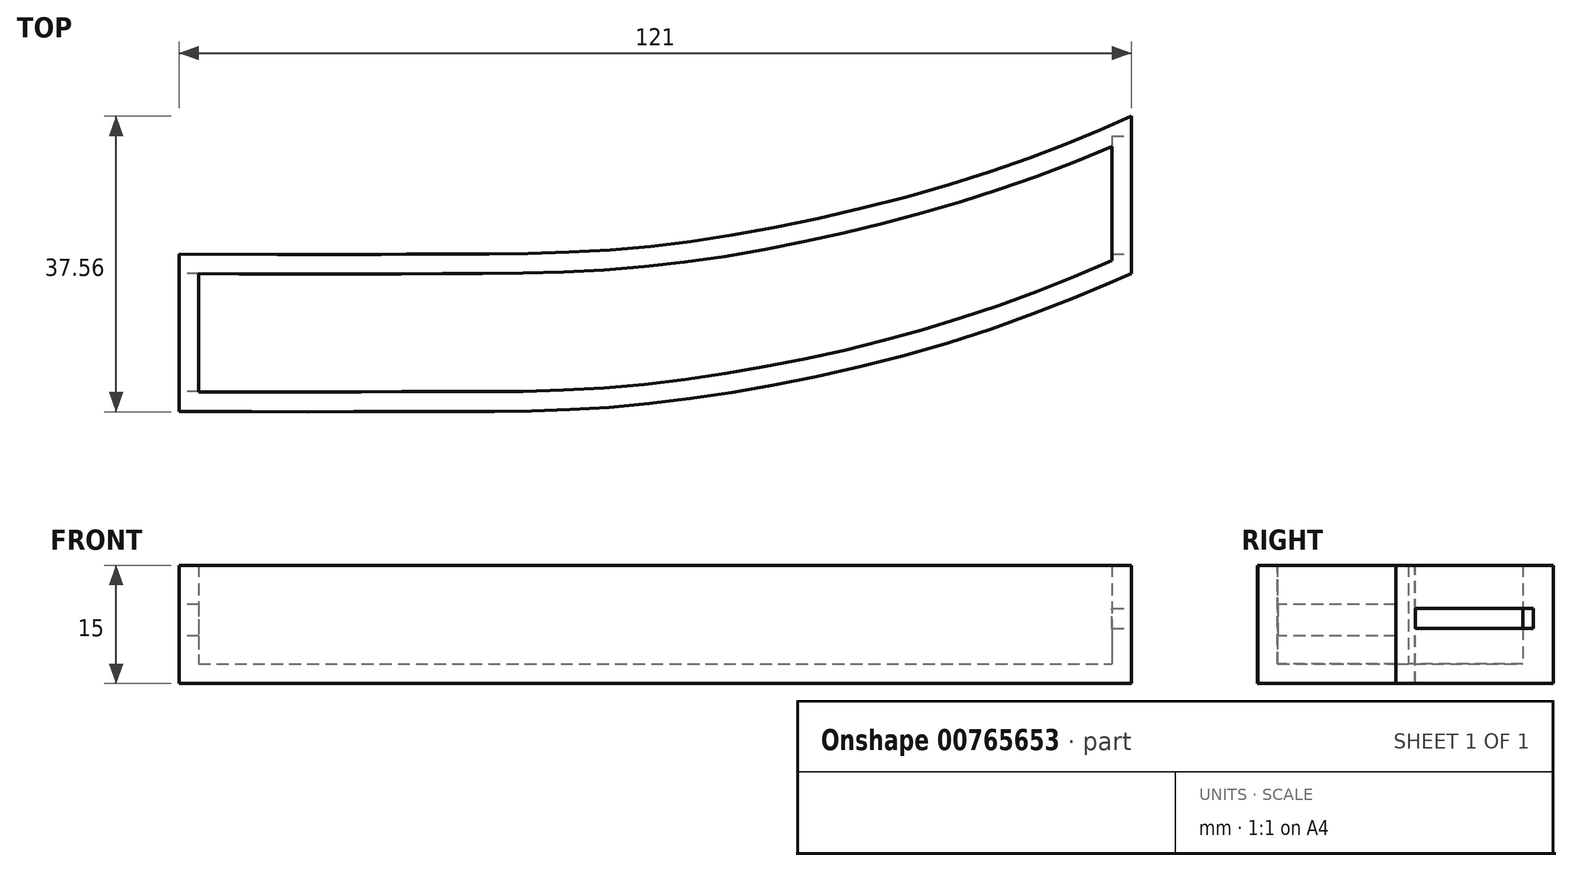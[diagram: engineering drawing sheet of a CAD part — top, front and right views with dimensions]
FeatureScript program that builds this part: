
annotation { "Feature Type Name" : "Feature", "Feature Type Description" : "" }
export const myFeature = defineFeature(function(context is Context, id is Id, definition is map)
    precondition{}
    {
        {
            var Q0;
            Q0=qCreatedBy(makeId("Top.planeOp"),FACE);
            var sketch = newSketch(context, id + "F0", { "sketchPlane" : qUnion([Q0])});
            skPoint(sketch, "E0.1.internal.orphan", {"position": v(32.6, 20) * mm});
            skPoint(sketch, "E0.2.internal.orphan", {"position": v(51.37, 20.3) * mm});
            skPoint(sketch, "E0.3.internal.orphan", {"position": v(102.14, 30.14) * mm});
            skPoint(sketch, "E0.5.internal.orphan", {"position": v(121, 37.5) * mm});
            skPoint(sketch, "E0.start.orphan", {"position": v(0, 20) * mm});
            skFitSpline(sketch, "E1", {"points": [v(0, 20) * mm, v(32.6, 20) * mm, v(51.37, 20.3) * mm, v(75, 23.23) * mm, v(102.14, 30.14) * mm, v(121, 37.5) * mm], "startDerivative": vector(347.02, -2.36) * mm, "endDerivative": vector(89.93, 40.6) * mm});
            skPoint(sketch, "E2.1.internal.orphan", {"position": v(32.6, 0) * mm});
            skPoint(sketch, "E2.2.internal.orphan", {"position": v(51.37, 0.3) * mm});
            skPoint(sketch, "E2.3.internal.orphan", {"position": v(102.14, 10.14) * mm});
            skPoint(sketch, "E2.5.internal.orphan", {"position": v(121, 17.5) * mm});
            skPoint(sketch, "E2.start.orphan", {"position": v(0, 0) * mm});
            skFitSpline(sketch, "E3", {"points": [v(0, 0) * mm, v(32.6, 0) * mm, v(51.37, 0.3) * mm, v(75, 3.23) * mm, v(102.14, 10.14) * mm, v(121, 17.5) * mm], "startDerivative": vector(239.64, -1.63) * mm, "endDerivative": vector(60.44, 27.24) * mm});
            skLineSegment(sketch, "E4", {"start": v(121, 37.5) * mm, "end": v(121, 17.5) * mm});
            skLineSegment(sketch, "E5", {"start": v(0, 20) * mm, "end": v(0, 0) * mm});
            skSolve(sketch);
        }
        {
            var Q0;
            Q0=makeQuery(id+"F0.imprint","IMPRINT",FACE,{"disambiguationData":[TD([[makeQuery(id+"F0.imprint","IMPRINT",EDGE,{"derivedFrom":sQuery(id+"F0.wireOp",EDGE,"E1")}),-1.0]])]});
            extrude(context, id + "F1", {"entities" : qUnion([Q0]), "depth" : 15 * mm, "offsetDistance" : 25 * mm});
        }
        {
            var Q0;
            Q0=makeQuery(id+"F1.opExtrude","CAP_FACE",FACE,{"disambiguationData":[OSD([sQuery(id+"F0.wireOp",EDGE,"E1"),sQuery(id+"F0.wireOp",EDGE,"E3"),sQuery(id+"F0.wireOp",EDGE,"E4"),sQuery(id+"F0.wireOp",EDGE,"E5")])],"isStart":false});
            shell(context, id + "F2", {"entities" : qUnion([Q0]), "thickness" : 2.5 * mm});
        }
        {
            var Q0;
            Q0=makeQuery(id+"F1.opExtrude","SWEPT_FACE",FACE,{"disambiguationData":[OSD([sQuery(id+"F0.wireOp",EDGE,"E5")])]});
            var sketch = newSketch(context, id + "F3", { "sketchPlane" : qUnion([Q0])});
            skLineSegment(sketch, "E6.bottom", {"start": v(-17.5, 10) * mm, "end": v(-2.5, 10) * mm});
            skLineSegment(sketch, "E6.top", {"start": v(-17.5, 6) * mm, "end": v(-2.5, 6) * mm});
            skLineSegment(sketch, "E6.left", {"start": v(-17.5, 10) * mm, "end": v(-17.5, 6) * mm});
            skLineSegment(sketch, "E6.right", {"start": v(-2.5, 10) * mm, "end": v(-2.5, 6) * mm});
            skSolve(sketch);
        }
        {
            var Q0;
            Q0=qSketchRegion(id+"F3",true);
            var Q1;
            Q1=makeQuery(id+"F2.opShell","OFFSET_FACE",FACE,{"disambiguationData":[OSD([sQuery(id+"F0.wireOp",EDGE,"E5")])]});
            extrude(context, id + "F4", {"entities" : qUnion([Q0]), "operationType" : NewBodyOperationType.REMOVE, "endBound" : BoundingType.UP_TO_SURFACE, "oppositeDirection" : true, "depth" : 25 * mm, "endBoundEntityFace" : qUnion([Q1]), "offsetDistance" : 25 * mm});
        }
        {
            var Q0;
            Q0=makeQuery(id+"F1.opExtrude","SWEPT_FACE",FACE,{"disambiguationData":[OSD([sQuery(id+"F0.wireOp",EDGE,"E4")])]});
            var sketch = newSketch(context, id + "F5", { "sketchPlane" : qUnion([Q0])});
            skLineSegment(sketch, "E7.bottom", {"start": v(20, 9.5) * mm, "end": v(35, 9.5) * mm});
            skLineSegment(sketch, "E7.top", {"start": v(20, 7) * mm, "end": v(35, 7) * mm});
            skLineSegment(sketch, "E7.left", {"start": v(20, 9.5) * mm, "end": v(20, 7) * mm});
            skLineSegment(sketch, "E7.right", {"start": v(35, 9.5) * mm, "end": v(35, 7) * mm});
            skSolve(sketch);
        }
        {
            var Q0;
            Q0=qSketchRegion(id+"F5",true);
            var Q1;
            Q1=makeQuery(id+"F2.opShell","OFFSET_FACE",FACE,{"disambiguationData":[OSD([sQuery(id+"F0.wireOp",EDGE,"E4")])]});
            extrude(context, id + "F6", {"entities" : qUnion([Q0]), "operationType" : NewBodyOperationType.REMOVE, "endBound" : BoundingType.UP_TO_SURFACE, "oppositeDirection" : true, "depth" : 25 * mm, "endBoundEntityFace" : qUnion([Q1]), "offsetDistance" : 25 * mm});
        }
    });
